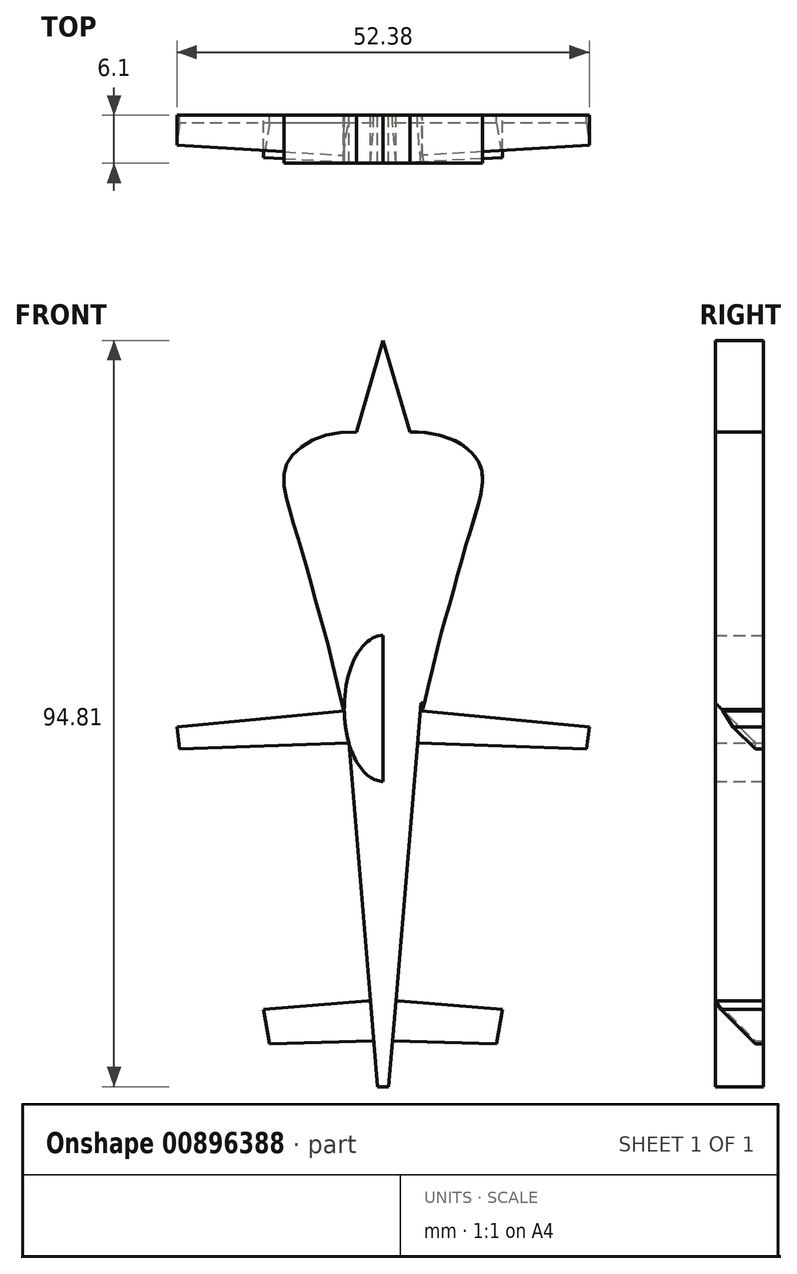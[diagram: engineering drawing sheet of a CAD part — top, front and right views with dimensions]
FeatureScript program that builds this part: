
annotation { "Feature Type Name" : "Feature", "Feature Type Description" : "" }
export const myFeature = defineFeature(function(context is Context, id is Id, definition is map)
    precondition{}
    {
        {
            var Q0;
            Q0=qCreatedBy(makeId("Front.planeOp"),FACE);
            var sketch = newSketch(context, id + "F0", { "sketchPlane" : qUnion([Q0])});
            skFitSpline(sketch, "E0", {"points": [v(0, 45.93) * mm, v(-6.84, 45.8) * mm, v(-11.14, 43.59) * mm, v(-12.57, 40.85) * mm, v(-12.05, 36.81) * mm, v(-10.49, 31.6) * mm, v(-8.54, 24.56) * mm, v(-6.71, 17.92) * mm, v(-5.02, 10.88) * mm, v(-5.02, 11.14) * mm], "startDerivative": vector(-53.03, 3.6) * mm, "endDerivative": vector(-1.07, 15.46) * mm});
            skEllipse(sketch, "E1", {"center": v(0, 11) * mm, "majorRadius": 9.27 * mm, "minorRadius": 4.94 * mm, "majorAxis": v(0, -1)});
            skFitSpline(sketch, "E2.MirrorCS", {"points": [v(0, 45.93) * mm, v(6.84, 45.8) * mm, v(11.14, 43.59) * mm, v(12.57, 40.85) * mm, v(12.05, 36.81) * mm, v(10.49, 31.6) * mm, v(8.54, 24.56) * mm, v(6.71, 17.92) * mm, v(5.02, 10.88) * mm, v(5.02, 11.14) * mm], "startDerivative": vector(53.03, 3.6) * mm, "endDerivative": vector(1.07, 15.46) * mm});
            skLineSegment(sketch, "E3", {"start": v(-4.36, 6.64) * mm, "end": v(-0.71, -37.05) * mm});
            skLineSegment(sketch, "E4.MirrorCS", {"start": v(4.36, 6.64) * mm, "end": v(0.71, -37.05) * mm});
            skLineSegment(sketch, "E5", {"start": v(-0.71, -37.05) * mm, "end": v(0.71, -37.05) * mm});
            skLineSegment(sketch, "E6", {"start": v(0, -37.05) * mm, "end": v(0, 45.93) * mm});
            skLineSegment(sketch, "E7", {"start": v(-5.02, 10.88) * mm, "end": v(-4.94, 10.7) * mm});
            skLineSegment(sketch, "E8", {"start": v(5.02, 10.88) * mm, "end": v(4.94, 10.7) * mm});
            skLineSegment(sketch, "E9", {"start": v(-4.94, 10.7) * mm, "end": v(-26.19, 8.65) * mm});
            skLineSegment(sketch, "E10", {"start": v(-26.19, 8.65) * mm, "end": v(-25.86, 5.85) * mm});
            skLineSegment(sketch, "E11", {"start": v(-25.86, 5.85) * mm, "end": v(-4.36, 6.64) * mm});
            skLineSegment(sketch, "E12.MirrorCS", {"start": v(4.94, 10.7) * mm, "end": v(26.19, 8.65) * mm});
            skLineSegment(sketch, "E13.MirrorCS", {"start": v(25.86, 5.85) * mm, "end": v(4.36, 6.64) * mm});
            skLineSegment(sketch, "E14.MirrorCS", {"start": v(26.19, 8.65) * mm, "end": v(25.86, 5.85) * mm});
            skLineSegment(sketch, "E15", {"start": v(-3.39, 46.1) * mm, "end": v(0, 57.76) * mm});
            skLineSegment(sketch, "E16.MirrorCS", {"start": v(3.39, 46.1) * mm, "end": v(0, 57.76) * mm});
            skLineSegment(sketch, "E17", {"start": v(-1.62, -26.13) * mm, "end": v(-15.17, -27.26) * mm});
            skLineSegment(sketch, "E18", {"start": v(-15.17, -27.26) * mm, "end": v(-14.4, -31.6) * mm});
            skLineSegment(sketch, "E19", {"start": v(-14.4, -31.6) * mm, "end": v(-1.2, -31.22) * mm});
            skLineSegment(sketch, "E20.MirrorCS", {"start": v(1.62, -26.13) * mm, "end": v(15.17, -27.26) * mm});
            skLineSegment(sketch, "E21.MirrorCS", {"start": v(14.4, -31.6) * mm, "end": v(1.2, -31.22) * mm});
            skLineSegment(sketch, "E22.MirrorCS", {"start": v(15.17, -27.26) * mm, "end": v(14.4, -31.6) * mm});
            skSolve(sketch);
        }
        {
            var Q0;
            {var subQ5=sQuery(id+"F0.wireOp",EDGE,"E7");Q0=makeQuery(id+"F0.imprint","IMPRINT",FACE,{"disambiguationData":[TD([[makeQuery(id+"F0.imprint","IMPRINT",EDGE,{"derivedFrom":subQ5}),1.0]])]});}
            var Q1;
            {var subQ5=sQuery(id+"F0.wireOp",EDGE,"E8");Q1=makeQuery(id+"F0.imprint","IMPRINT",FACE,{"disambiguationData":[TD([[makeQuery(id+"F0.imprint","IMPRINT",EDGE,{"derivedFrom":subQ5}),-1.0]])]});}
            var Q2;
            {var subQ3=sQuery(id+"F0.wireOp",EDGE,"E15");Q2=makeQuery(id+"F0.imprint","IMPRINT",FACE,{"disambiguationData":[TD([[makeQuery(id+"F0.imprint","IMPRINT",EDGE,{"derivedFrom":subQ3}),-1.0]])]});}
            var Q3;
            {var subQ0=sQuery(id+"F0.wireOp",EDGE,"E1");var subQ2=sQuery(id+"F0.wireOp",EDGE,"E6");var subQ5=makeQuery(id+"F0.imprint","INTERSECT",VERTEX,{"disambiguationData":[OD(0.0)],"derivedFrom":[subQ0,subQ2]});Q3=makeQuery(id+"F0.imprint","IMPRINT",FACE,{"disambiguationData":[TD([[makeQuery(id+"F0.imprint","IMPRINT",EDGE,{"disambiguationData":[TD([[subQ5,-1.0]])],"derivedFrom":subQ2}),1.0]])]});}
            var Q4;
            {var subQ0=sQuery(id+"F0.wireOp",EDGE,"E1");var subQ1=makeQuery(id+"F0.imprint","INTERSECT",VERTEX,{"derivedFrom":[subQ0,sQuery(id+"F0.wireOp",EDGE,"E8")]});Q4=makeQuery(id+"F0.imprint","IMPRINT",FACE,{"disambiguationData":[TD([[makeQuery(id+"F0.imprint","IMPRINT",EDGE,{"disambiguationData":[TD([[subQ1,1.0]])],"derivedFrom":subQ0}),1.0]])]});}
            var Q5;
            {var subQ2=sQuery(id+"F0.wireOp",EDGE,"E12.MirrorCS");Q5=makeQuery(id+"F0.imprint","IMPRINT",FACE,{"disambiguationData":[TD([[makeQuery(id+"F0.imprint","IMPRINT",EDGE,{"derivedFrom":subQ2}),-1.0]])]});}
            var Q6;
            {var subQ2=sQuery(id+"F0.wireOp",EDGE,"E9");Q6=makeQuery(id+"F0.imprint","IMPRINT",FACE,{"disambiguationData":[TD([[makeQuery(id+"F0.imprint","IMPRINT",EDGE,{"derivedFrom":subQ2}),1.0]])]});}
            var Q7;
            {var subQ0=sQuery(id+"F0.wireOp",EDGE,"E3");var subQ1=makeQuery(id+"F0.imprint","INTERSECT",VERTEX,{"derivedFrom":[subQ0,sQuery(id+"F0.wireOp",EDGE,"E17")]});Q7=makeQuery(id+"F0.imprint","IMPRINT",FACE,{"disambiguationData":[TD([[makeQuery(id+"F0.imprint","IMPRINT",EDGE,{"disambiguationData":[TD([[subQ1,-1.0]])],"derivedFrom":subQ0}),1.0]])]});}
            var Q8;
            {var subQ1=sQuery(id+"F0.wireOp",EDGE,"E4.MirrorCS");var subQ4=makeQuery(id+"F0.imprint","INTERSECT",VERTEX,{"derivedFrom":[subQ1,sQuery(id+"F0.wireOp",EDGE,"E20.MirrorCS")]});Q8=makeQuery(id+"F0.imprint","IMPRINT",FACE,{"disambiguationData":[TD([[makeQuery(id+"F0.imprint","IMPRINT",EDGE,{"disambiguationData":[TD([[subQ4,-1.0]])],"derivedFrom":subQ1}),-1.0]])]});}
            var Q9;
            {var subQ0=sQuery(id+"F0.wireOp",EDGE,"E20.MirrorCS");Q9=makeQuery(id+"F0.imprint","IMPRINT",FACE,{"disambiguationData":[TD([[makeQuery(id+"F0.imprint","IMPRINT",EDGE,{"derivedFrom":subQ0}),-1.0]])]});}
            var Q10;
            {var subQ0=sQuery(id+"F0.wireOp",EDGE,"E17");Q10=makeQuery(id+"F0.imprint","IMPRINT",FACE,{"disambiguationData":[TD([[makeQuery(id+"F0.imprint","IMPRINT",EDGE,{"derivedFrom":subQ0}),1.0]])]});}
            extrude(context, id + "F1", {"entities" : qUnion([Q0, Q1, Q2, Q3, Q4, Q5, Q6, Q7, Q8, Q9, Q10]), "depth" : 6.1 * mm, "offsetDistance" : 25.4 * mm});
        }
        {
            var Q0;
            Q0=makeQuery(id+"F1.opExtrude","CAP_EDGE",EDGE,{"disambiguationData":[OSD([sQuery(id+"F0.wireOp",EDGE,"E11")])],"isStart":false});
            chamfer(context, id + "F2", {"entities" : qUnion([Q0]), "width" : 5.08 * mm, "tangentPropagation" : true});
        }
        {
            var Q0;
            Q0=makeQuery(id+"F1.opExtrude","CAP_EDGE",EDGE,{"disambiguationData":[OSD([sQuery(id+"F0.wireOp",EDGE,"E13.MirrorCS")])],"isStart":false});
            chamfer(context, id + "F3", {"entities" : qUnion([Q0]), "width" : 5.08 * mm, "tangentPropagation" : true});
        }
        {
            var Q0;
            Q0=makeQuery(id+"F1.opExtrude","CAP_EDGE",EDGE,{"disambiguationData":[OSD([sQuery(id+"F0.wireOp",EDGE,"E19")])],"isStart":false});
            chamfer(context, id + "F4", {"entities" : qUnion([Q0]), "width" : 5.08 * mm, "tangentPropagation" : true});
        }
        {
            var Q0;
            Q0=makeQuery(id+"F1.opExtrude","CAP_EDGE",EDGE,{"disambiguationData":[OSD([sQuery(id+"F0.wireOp",EDGE,"E21.MirrorCS")])],"isStart":false});
            chamfer(context, id + "F5", {"entities" : qUnion([Q0]), "width" : 5.08 * mm, "tangentPropagation" : true});
        }
    });
